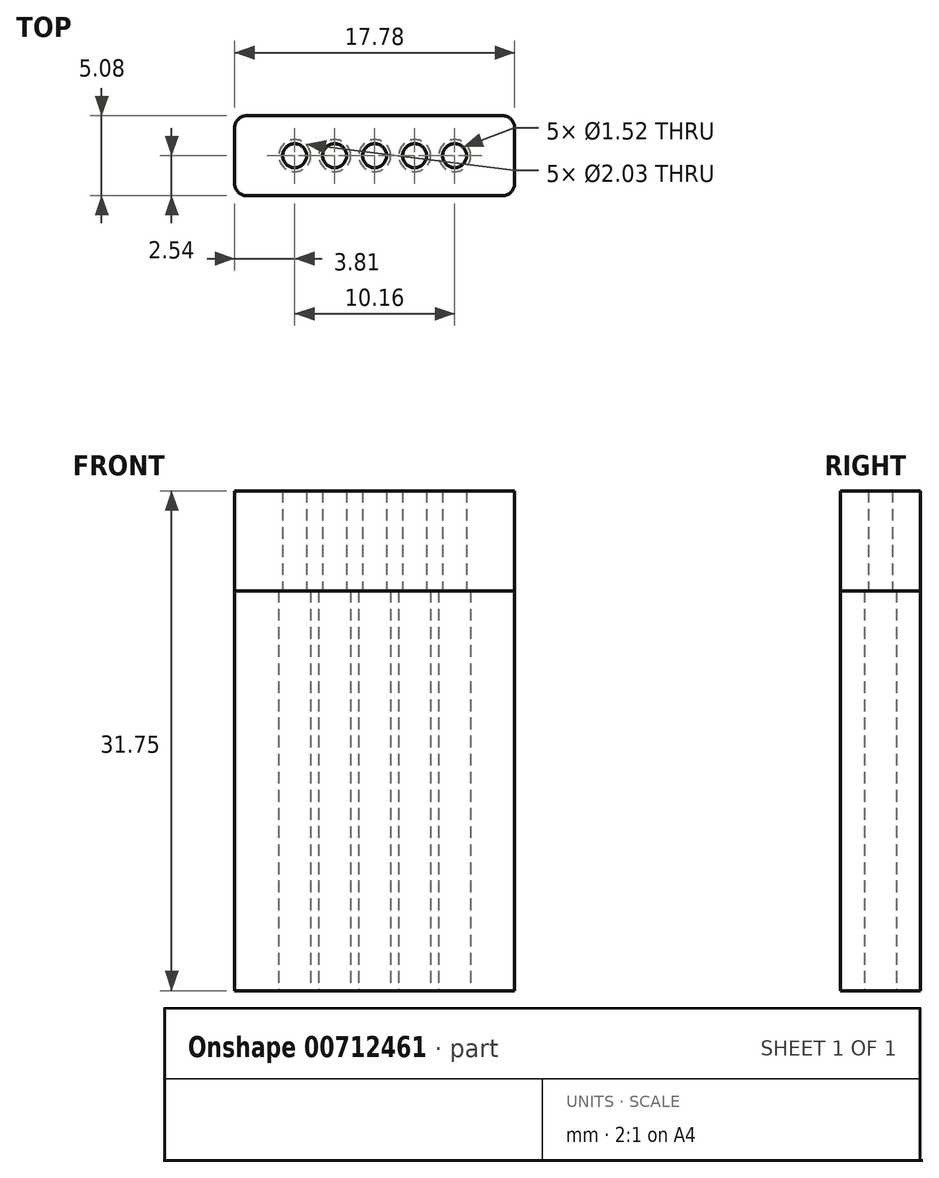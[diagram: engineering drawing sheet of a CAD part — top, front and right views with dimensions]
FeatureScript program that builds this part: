
annotation { "Feature Type Name" : "Feature", "Feature Type Description" : "" }
export const myFeature = defineFeature(function(context is Context, id is Id, definition is map)
    precondition{}
    {
        {
            var Q0;
            Q0=qCreatedBy(makeId("Top.planeOp"),FACE);
            var sketch = newSketch(context, id + "F0", { "sketchPlane" : qUnion([Q0])});
            skLineSegment(sketch, "E0.bottom", {"start": v(8.13, -2.54) * mm, "end": v(-8.13, -2.54) * mm});
            skLineSegment(sketch, "E0.top", {"start": v(8.13, 2.54) * mm, "end": v(-8.13, 2.54) * mm});
            skLineSegment(sketch, "E0.left", {"start": v(8.9, -1.78) * mm, "end": v(8.9, 1.78) * mm});
            skLineSegment(sketch, "E0.right", {"start": v(-8.9, -1.78) * mm, "end": v(-8.9, 1.78) * mm});
            skPoint(sketch, "E0.middle", {"position": v(0, 0) * mm});
            skCircle(sketch, "E1", {"center": v(0, 0) * mm, "radius": 1.02 * mm});
            skCircle(sketch, "E2.1.0.0", {"center": v(2.54, 0) * mm, "radius": 1.02 * mm});
            skCircle(sketch, "E2.2.0.0", {"center": v(5.08, 0) * mm, "radius": 1.02 * mm});
            skLineSegment(sketch, "E2.direction1", {"start": v(0, 0) * mm, "end": v(2.54, 0) * mm, "construction": true});
            skCircle(sketch, "E3.1.0.0", {"center": v(-2.54, 0) * mm, "radius": 1.02 * mm});
            skCircle(sketch, "E3.2.0.0", {"center": v(-5.08, 0) * mm, "radius": 1.02 * mm});
            skLineSegment(sketch, "E3.direction1", {"start": v(0, 0) * mm, "end": v(-2.54, 0) * mm, "construction": true});
            skPoint(sketch, "E4.visualSharp", {"position": v(-8.9, 2.54) * mm});
            skArc(sketch, "E4.filletArc", {"start": v(-8.13, 2.54) * mm, "mid": v(-8.67, 2.32) * mm, "end": v(-8.9, 1.78) * mm});
            skPoint(sketch, "E5.visualSharp", {"position": v(8.9, 2.54) * mm});
            skArc(sketch, "E5.filletArc", {"start": v(8.9, 1.78) * mm, "mid": v(8.67, 2.32) * mm, "end": v(8.13, 2.54) * mm});
            skPoint(sketch, "E6.visualSharp", {"position": v(8.9, -2.54) * mm});
            skArc(sketch, "E6.filletArc", {"start": v(8.13, -2.54) * mm, "mid": v(8.67, -2.32) * mm, "end": v(8.9, -1.78) * mm});
            skPoint(sketch, "E7.visualSharp", {"position": v(-8.9, -2.54) * mm});
            skArc(sketch, "E7.filletArc", {"start": v(-8.9, -1.78) * mm, "mid": v(-8.67, -2.32) * mm, "end": v(-8.13, -2.54) * mm});
            skSolve(sketch);
        }
        {
            var Q0;
            Q0=makeQuery(id+"F0.imprint","IMPRINT",FACE,{"disambiguationData":[TD([[makeQuery(id+"F0.imprint","IMPRINT",EDGE,{"derivedFrom":sQuery(id+"F0.wireOp",EDGE,"E0.bottom")}),-1.0]])]});
            extrude(context, id + "F1", {"entities" : qUnion([Q0]), "depth" : 25.4 * mm});
        }
        {
            var Q0;
            Q0=makeQuery(id+"F1.opExtrude","CAP_FACE",FACE,{"disambiguationData":[OSD([sQuery(id+"F0.wireOp",EDGE,"E0.bottom"),sQuery(id+"F0.wireOp",EDGE,"E0.top"),sQuery(id+"F0.wireOp",EDGE,"E0.left"),sQuery(id+"F0.wireOp",EDGE,"E0.right"),sQuery(id+"F0.wireOp",EDGE,"E1"),sQuery(id+"F0.wireOp",EDGE,"E2.1.0.0"),sQuery(id+"F0.wireOp",EDGE,"E2.2.0.0"),sQuery(id+"F0.wireOp",EDGE,"E3.1.0.0"),sQuery(id+"F0.wireOp",EDGE,"E3.2.0.0"),sQuery(id+"F0.wireOp",EDGE,"E4.filletArc"),sQuery(id+"F0.wireOp",EDGE,"E5.filletArc"),sQuery(id+"F0.wireOp",EDGE,"E6.filletArc"),sQuery(id+"F0.wireOp",EDGE,"E7.filletArc")])],"isStart":false});
            var sketch = newSketch(context, id + "F2", { "sketchPlane" : qUnion([Q0])});
            skLineSegment(sketch, "E8.0", {"start": v(8.13, 2.54) * mm, "end": v(-8.13, 2.54) * mm});
            skArc(sketch, "E9.0", {"start": v(-8.13, 2.54) * mm, "mid": v(-8.67, 2.32) * mm, "end": v(-8.9, 1.78) * mm});
            skLineSegment(sketch, "E10.0", {"start": v(-8.9, -1.78) * mm, "end": v(-8.9, 1.78) * mm});
            skArc(sketch, "E11.0", {"start": v(-8.9, -1.78) * mm, "mid": v(-8.67, -2.32) * mm, "end": v(-8.13, -2.54) * mm});
            skLineSegment(sketch, "E12.0", {"start": v(8.13, -2.54) * mm, "end": v(-8.13, -2.54) * mm});
            skArc(sketch, "E13.0", {"start": v(8.13, -2.54) * mm, "mid": v(8.67, -2.32) * mm, "end": v(8.9, -1.78) * mm});
            skLineSegment(sketch, "E14.0", {"start": v(8.9, -1.78) * mm, "end": v(8.9, 1.78) * mm});
            skPoint(sketch, "E15.0", {"position": v(8.67, 2.32) * mm});
            skArc(sketch, "E16.0", {"start": v(8.9, 1.78) * mm, "mid": v(8.67, 2.32) * mm, "end": v(8.13, 2.54) * mm});
            skPoint(sketch, "E17", {"position": v(-5.08, 0) * mm});
            skPoint(sketch, "E18", {"position": v(-2.54, 0) * mm});
            skPoint(sketch, "E19", {"position": v(0, 0) * mm});
            skPoint(sketch, "E20", {"position": v(2.54, 0) * mm});
            skPoint(sketch, "E21", {"position": v(5.08, 0) * mm});
            skCircle(sketch, "E22", {"center": v(-5.08, 0) * mm, "radius": 0.76 * mm});
            skCircle(sketch, "E23.1.0.0", {"center": v(-2.54, 0) * mm, "radius": 0.76 * mm});
            skCircle(sketch, "E23.2.0.0", {"center": v(0, 0) * mm, "radius": 0.76 * mm});
            skCircle(sketch, "E23.3.0.0", {"center": v(2.54, 0) * mm, "radius": 0.76 * mm});
            skCircle(sketch, "E23.4.0.0", {"center": v(5.08, 0) * mm, "radius": 0.76 * mm});
            skLineSegment(sketch, "E23.direction1", {"start": v(-5.08, 0) * mm, "end": v(-2.54, 0) * mm, "construction": true});
            skSolve(sketch);
        }
        {
            var Q0;
            Q0=qSketchRegion(id+"F2",true);
            extrude(context, id + "F3", {"entities" : qUnion([Q0]), "depth" : 6.35 * mm});
        }
    });
